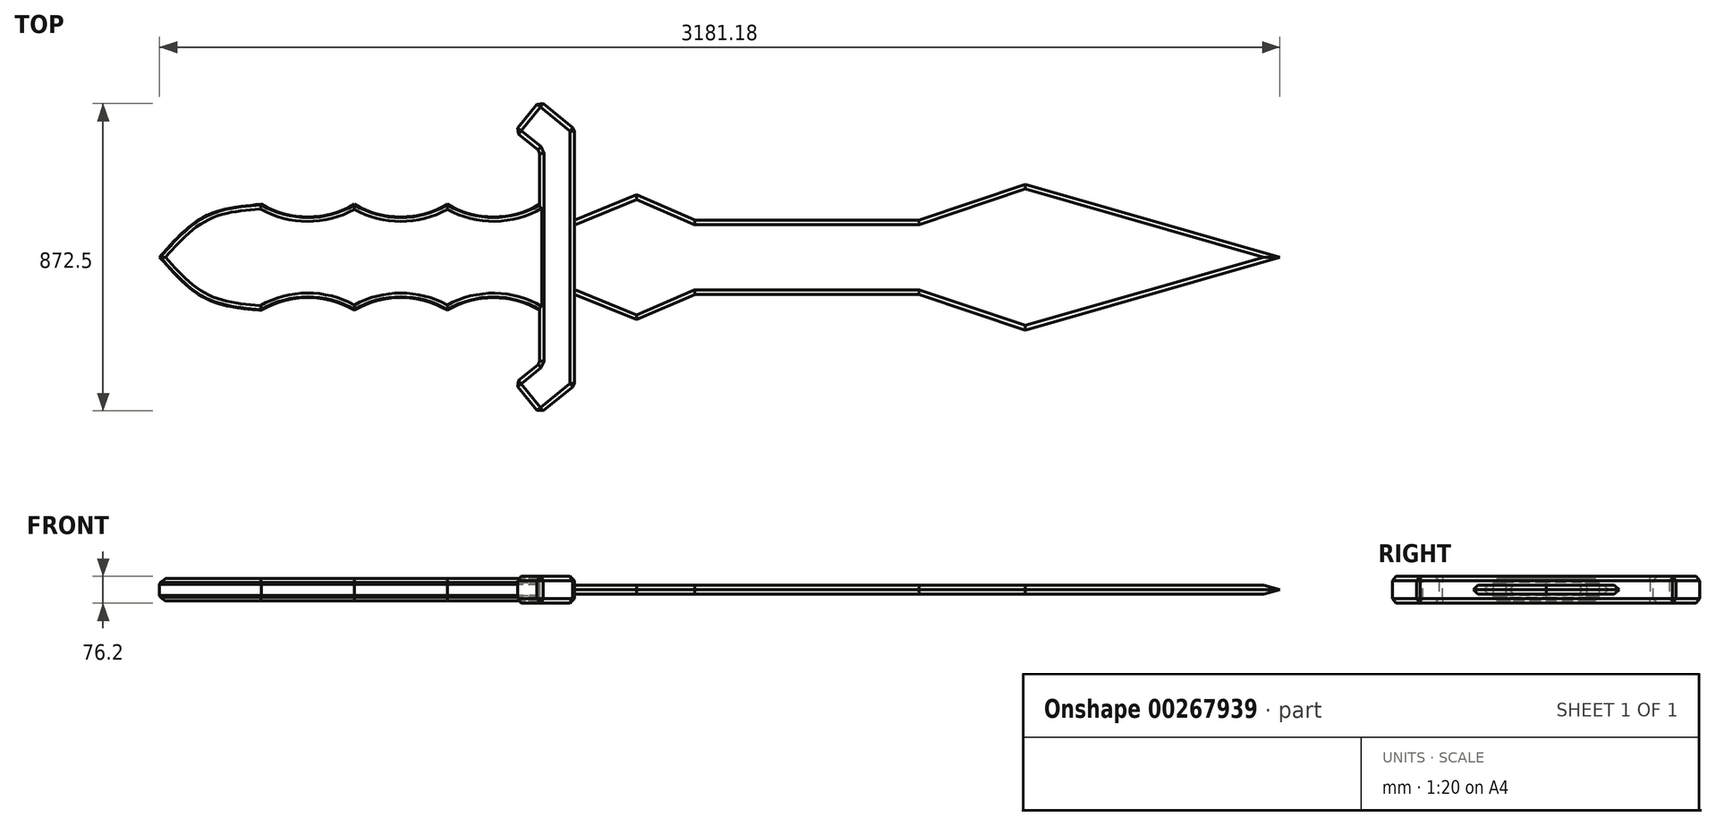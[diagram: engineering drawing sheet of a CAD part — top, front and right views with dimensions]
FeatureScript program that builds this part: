
annotation { "Feature Type Name" : "Feature", "Feature Type Description" : "" }
export const myFeature = defineFeature(function(context is Context, id is Id, definition is map)
    precondition{}
    {
        {
            var Q0;
            Q0=qCreatedBy(makeId("Top.planeOp"),FACE);
            var sketch = newSketch(context, id + "F0", { "sketchPlane" : qUnion([Q0])});
            skLineSegment(sketch, "E0", {"start": v(-1336.98, 0) * mm, "end": v(2042.28, 0) * mm, "construction": true});
            skLineSegment(sketch, "E1", {"start": v(2042.28, 0) * mm, "end": v(1319.26, 207.04) * mm});
            skLineSegment(sketch, "E2", {"start": v(1319.26, 207.04) * mm, "end": v(1016.82, 105.17) * mm});
            skLineSegment(sketch, "E3", {"start": v(1016.82, 105.17) * mm, "end": v(382.56, 105.17) * mm});
            skLineSegment(sketch, "E4", {"start": v(382.56, 105.17) * mm, "end": v(216.1, 177.22) * mm});
            skLineSegment(sketch, "E5", {"start": v(216.1, 177.22) * mm, "end": v(39.37, 105.17) * mm});
            skLineSegment(sketch, "E6", {"start": v(39.37, 105.17) * mm, "end": v(39.37, 0) * mm});
            skLineSegment(sketch, "E7", {"start": v(39.37, 105.17) * mm, "end": v(39.37, 364.38) * mm});
            skLineSegment(sketch, "E8", {"start": v(39.37, 364.38) * mm, "end": v(-59.33, 444.24) * mm});
            skLineSegment(sketch, "E9", {"start": v(-59.33, 444.24) * mm, "end": v(-129.5, 357.5) * mm});
            skLineSegment(sketch, "E10", {"start": v(-129.5, 357.5) * mm, "end": v(-59.33, 300.73) * mm});
            skLineSegment(sketch, "E11", {"start": v(-59.33, 300.73) * mm, "end": v(-59.33, 0) * mm});
            skArc(sketch, "E12", {"start": v(-321.86, 150.37) * mm, "mid": v(-190.6, 114.69) * mm, "end": v(-59.33, 150.37) * mm});
            skPoint(sketch, "E12.startSnap0", {"position": v(-59.33, 150.37) * mm});
            skArc(sketch, "E13", {"start": v(-585.75, 150.37) * mm, "mid": v(-453.8, 114.34) * mm, "end": v(-321.86, 150.37) * mm});
            skArc(sketch, "E14", {"start": v(-849.64, 150.37) * mm, "mid": v(-717.7, 114.34) * mm, "end": v(-585.75, 150.37) * mm});
            skLineSegment(sketch, "E15", {"start": v(-190.6, 374) * mm, "end": v(-1033.32, 374) * mm, "construction": true});
            skFitSpline(sketch, "E16", {"points": [v(-849.64, 150.37) * mm, v(-1008.23, 117.05) * mm, v(-1138.9, 0) * mm], "startDerivative": vector(-340.1, -28.4) * mm, "endDerivative": vector(-239.1, -270.74) * mm});
            skLineSegment(sketch, "E17.MirrorCS", {"start": v(1016.82, -105.17) * mm, "end": v(382.56, -105.17) * mm});
            skLineSegment(sketch, "E18.MirrorCS", {"start": v(1319.26, -207.04) * mm, "end": v(1016.82, -105.17) * mm});
            skLineSegment(sketch, "E19.MirrorCS", {"start": v(2042.28, 0) * mm, "end": v(1319.26, -207.04) * mm});
            skLineSegment(sketch, "E20.MirrorCS", {"start": v(216.1, -177.22) * mm, "end": v(39.37, -105.17) * mm});
            skLineSegment(sketch, "E21.MirrorCS", {"start": v(382.56, -105.17) * mm, "end": v(216.1, -177.22) * mm});
            skLineSegment(sketch, "E22.MirrorCS", {"start": v(39.37, -105.17) * mm, "end": v(39.37, 0) * mm});
            skLineSegment(sketch, "E23.MirrorCS", {"start": v(-59.33, -300.73) * mm, "end": v(-59.33, 0) * mm});
            skLineSegment(sketch, "E24.MirrorCS", {"start": v(39.37, -105.17) * mm, "end": v(39.37, -364.38) * mm});
            skLineSegment(sketch, "E25.MirrorCS", {"start": v(-129.5, -357.5) * mm, "end": v(-59.33, -300.73) * mm});
            skLineSegment(sketch, "E26.MirrorCS", {"start": v(-59.33, -444.24) * mm, "end": v(-129.5, -357.5) * mm});
            skLineSegment(sketch, "E27.MirrorCS", {"start": v(39.37, -364.38) * mm, "end": v(-59.33, -444.24) * mm});
            skArc(sketch, "E28.MirrorCS", {"start": v(-321.86, -150.37) * mm, "mid": v(-190.6, -114.69) * mm, "end": v(-59.33, -150.37) * mm});
            skArc(sketch, "E29.MirrorCS", {"start": v(-585.75, -150.37) * mm, "mid": v(-453.8, -114.34) * mm, "end": v(-321.86, -150.37) * mm});
            skArc(sketch, "E30.MirrorCS", {"start": v(-849.64, -150.37) * mm, "mid": v(-717.7, -114.34) * mm, "end": v(-585.75, -150.37) * mm});
            skFitSpline(sketch, "E31.MirrorCS", {"points": [v(-849.64, -150.37) * mm, v(-1008.23, -117.05) * mm, v(-1138.9, 0) * mm], "startDerivative": vector(-340.1, 28.4) * mm, "endDerivative": vector(-239.1, 270.74) * mm});
            skSolve(sketch);
        }
        {
            var Q0;
            Q0=makeQuery(id+"F0.imprint","IMPRINT",FACE,{"disambiguationData":[TD([[makeQuery(id+"F0.imprint","IMPRINT",EDGE,{"derivedFrom":sQuery(id+"F0.wireOp",EDGE,"E6")}),-1.0]])]});
            extrude(context, id + "F1", {"entities" : qUnion([Q0]), "depth" : 38.1 * mm, "hasSecondDirection" : true, "secondDirectionOppositeDirection" : true, "secondDirectionDepth" : 38.1 * mm});
        }
        {
            var Q0;
            {var subQ4=sQuery(id+"F0.wireOp",EDGE,"E12");Q0=makeQuery(id+"F0.imprint","IMPRINT",FACE,{"disambiguationData":[TD([[makeQuery(id+"F0.imprint","IMPRINT",EDGE,{"derivedFrom":subQ4}),-1.0]])]});}
            extrude(context, id + "F2", {"entities" : qUnion([Q0]), "operationType" : NewBodyOperationType.ADD, "depth" : 31.75 * mm, "hasSecondDirection" : true, "secondDirectionOppositeDirection" : true, "secondDirectionDepth" : 31.75 * mm});
        }
        {
            var Q0;
            Q0=makeQuery(id+"F0.imprint","IMPRINT",FACE,{"disambiguationData":[TD([[makeQuery(id+"F0.imprint","IMPRINT",EDGE,{"derivedFrom":sQuery(id+"F0.wireOp",EDGE,"E1")}),1.0]])]});
            extrude(context, id + "F3", {"entities" : qUnion([Q0]), "operationType" : NewBodyOperationType.ADD, "depth" : 12.7 * mm, "hasSecondDirection" : true, "secondDirectionOppositeDirection" : true, "secondDirectionDepth" : 12.7 * mm});
        }
        {
            var Q0;
            Q0=makeQuery(id+"F3.opExtrude","CAP_EDGE",EDGE,{"disambiguationData":[OSD([sQuery(id+"F0.wireOp",EDGE,"E5")])],"isStart":false});
            var Q1;
            Q1=makeQuery(id+"F3.opExtrude","CAP_EDGE",EDGE,{"disambiguationData":[OSD([sQuery(id+"F0.wireOp",EDGE,"E4")])],"isStart":false});
            var Q2;
            Q2=makeQuery(id+"F3.opExtrude","CAP_EDGE",EDGE,{"disambiguationData":[OSD([sQuery(id+"F0.wireOp",EDGE,"E3")])],"isStart":false});
            var Q3;
            Q3=makeQuery(id+"F3.opExtrude","CAP_EDGE",EDGE,{"disambiguationData":[OSD([sQuery(id+"F0.wireOp",EDGE,"E2")])],"isStart":false});
            var Q4;
            Q4=makeQuery(id+"F3.opExtrude","CAP_EDGE",EDGE,{"disambiguationData":[OSD([sQuery(id+"F0.wireOp",EDGE,"E1")])],"isStart":false});
            var Q5;
            Q5=makeQuery(id+"F3.opExtrude","CAP_EDGE",EDGE,{"disambiguationData":[OSD([sQuery(id+"F0.wireOp",EDGE,"E19.MirrorCS")])],"isStart":false});
            var Q6;
            Q6=makeQuery(id+"F3.opExtrude","CAP_EDGE",EDGE,{"disambiguationData":[OSD([sQuery(id+"F0.wireOp",EDGE,"E18.MirrorCS")])],"isStart":false});
            var Q7;
            Q7=makeQuery(id+"F3.opExtrude","CAP_EDGE",EDGE,{"disambiguationData":[OSD([sQuery(id+"F0.wireOp",EDGE,"E21.MirrorCS")])],"isStart":false});
            var Q8;
            Q8=makeQuery(id+"F3.opExtrude","CAP_EDGE",EDGE,{"disambiguationData":[OSD([sQuery(id+"F0.wireOp",EDGE,"E20.MirrorCS")])],"isStart":true});
            var Q9;
            Q9=makeQuery(id+"F3.opExtrude","CAP_EDGE",EDGE,{"disambiguationData":[OSD([sQuery(id+"F0.wireOp",EDGE,"E20.MirrorCS")])],"isStart":false});
            var Q10;
            Q10=makeQuery(id+"F3.opExtrude","CAP_EDGE",EDGE,{"disambiguationData":[OSD([sQuery(id+"F0.wireOp",EDGE,"E21.MirrorCS")])],"isStart":true});
            var Q11;
            Q11=makeQuery(id+"F3.opExtrude","CAP_EDGE",EDGE,{"disambiguationData":[OSD([sQuery(id+"F0.wireOp",EDGE,"E17.MirrorCS")])],"isStart":false});
            var Q12;
            Q12=makeQuery(id+"F3.opExtrude","CAP_EDGE",EDGE,{"disambiguationData":[OSD([sQuery(id+"F0.wireOp",EDGE,"E17.MirrorCS")])],"isStart":true});
            var Q13;
            Q13=makeQuery(id+"F3.opExtrude","CAP_EDGE",EDGE,{"disambiguationData":[OSD([sQuery(id+"F0.wireOp",EDGE,"E18.MirrorCS")])],"isStart":true});
            var Q14;
            Q14=makeQuery(id+"F3.opExtrude","CAP_EDGE",EDGE,{"disambiguationData":[OSD([sQuery(id+"F0.wireOp",EDGE,"E19.MirrorCS")])],"isStart":true});
            var Q15;
            Q15=makeQuery(id+"F3.opExtrude","CAP_EDGE",EDGE,{"disambiguationData":[OSD([sQuery(id+"F0.wireOp",EDGE,"E4")])],"isStart":true});
            var Q16;
            Q16=makeQuery(id+"F3.opExtrude","CAP_EDGE",EDGE,{"disambiguationData":[OSD([sQuery(id+"F0.wireOp",EDGE,"E5")])],"isStart":true});
            var Q17;
            Q17=makeQuery(id+"F3.opExtrude","CAP_EDGE",EDGE,{"disambiguationData":[OSD([sQuery(id+"F0.wireOp",EDGE,"E3")])],"isStart":true});
            var Q18;
            Q18=makeQuery(id+"F3.opExtrude","CAP_EDGE",EDGE,{"disambiguationData":[OSD([sQuery(id+"F0.wireOp",EDGE,"E2")])],"isStart":true});
            var Q19;
            Q19=makeQuery(id+"F3.opExtrude","CAP_EDGE",EDGE,{"disambiguationData":[OSD([sQuery(id+"F0.wireOp",EDGE,"E1")])],"isStart":true});
            chamfer(context, id + "F4", {"entities" : qUnion([Q0, Q1, Q2, Q3, Q4, Q5, Q6, Q7, Q8, Q9, Q10, Q11, Q12, Q13, Q14, Q15, Q16, Q17, Q18, Q19]), "width" : 12.7 * mm, "tangentPropagation" : true});
        }
        {
            var Q0;
            Q0=makeQuery(id+"F1.opExtrude","CAP_EDGE",EDGE,{"disambiguationData":[OSD([sQuery(id+"F0.wireOp",EDGE,"E11"),sQuery(id+"F0.wireOp",EDGE,"E23.MirrorCS")])],"isStart":false});
            var Q1;
            Q1=makeQuery(id+"F1.opExtrude","CAP_EDGE",EDGE,{"disambiguationData":[OSD([sQuery(id+"F0.wireOp",EDGE,"E10")])],"isStart":false});
            var Q2;
            Q2=makeQuery(id+"F1.opExtrude","CAP_EDGE",EDGE,{"disambiguationData":[OSD([sQuery(id+"F0.wireOp",EDGE,"E9")])],"isStart":false});
            var Q3;
            Q3=makeQuery(id+"F1.opExtrude","CAP_EDGE",EDGE,{"disambiguationData":[OSD([sQuery(id+"F0.wireOp",EDGE,"E8")])],"isStart":false});
            var Q4;
            Q4=makeQuery(id+"F1.opExtrude","CAP_EDGE",EDGE,{"disambiguationData":[OSD([sQuery(id+"F0.wireOp",EDGE,"E6"),sQuery(id+"F0.wireOp",EDGE,"E7"),sQuery(id+"F0.wireOp",EDGE,"E22.MirrorCS"),sQuery(id+"F0.wireOp",EDGE,"E24.MirrorCS")])],"isStart":false});
            var Q5;
            Q5=makeQuery(id+"F1.opExtrude","CAP_EDGE",EDGE,{"disambiguationData":[OSD([sQuery(id+"F0.wireOp",EDGE,"E25.MirrorCS")])],"isStart":false});
            var Q6;
            Q6=makeQuery(id+"F1.opExtrude","CAP_EDGE",EDGE,{"disambiguationData":[OSD([sQuery(id+"F0.wireOp",EDGE,"E26.MirrorCS")])],"isStart":false});
            var Q7;
            Q7=makeQuery(id+"F1.opExtrude","CAP_EDGE",EDGE,{"disambiguationData":[OSD([sQuery(id+"F0.wireOp",EDGE,"E27.MirrorCS")])],"isStart":false});
            var Q8;
            Q8=makeQuery(id+"F1.opExtrude","CAP_EDGE",EDGE,{"disambiguationData":[OSD([sQuery(id+"F0.wireOp",EDGE,"E27.MirrorCS")])],"isStart":true});
            var Q9;
            Q9=makeQuery(id+"F1.opExtrude","CAP_EDGE",EDGE,{"disambiguationData":[OSD([sQuery(id+"F0.wireOp",EDGE,"E26.MirrorCS")])],"isStart":true});
            var Q10;
            Q10=makeQuery(id+"F1.opExtrude","CAP_EDGE",EDGE,{"disambiguationData":[OSD([sQuery(id+"F0.wireOp",EDGE,"E6"),sQuery(id+"F0.wireOp",EDGE,"E7"),sQuery(id+"F0.wireOp",EDGE,"E22.MirrorCS"),sQuery(id+"F0.wireOp",EDGE,"E24.MirrorCS")])],"isStart":true});
            var Q11;
            Q11=makeQuery(id+"F1.opExtrude","CAP_EDGE",EDGE,{"disambiguationData":[OSD([sQuery(id+"F0.wireOp",EDGE,"E25.MirrorCS")])],"isStart":true});
            var Q12;
            Q12=makeQuery(id+"F1.opExtrude","CAP_EDGE",EDGE,{"disambiguationData":[OSD([sQuery(id+"F0.wireOp",EDGE,"E11"),sQuery(id+"F0.wireOp",EDGE,"E23.MirrorCS")])],"isStart":true});
            var Q13;
            Q13=makeQuery(id+"F1.opExtrude","CAP_EDGE",EDGE,{"disambiguationData":[OSD([sQuery(id+"F0.wireOp",EDGE,"E10")])],"isStart":true});
            var Q14;
            Q14=makeQuery(id+"F1.opExtrude","CAP_EDGE",EDGE,{"disambiguationData":[OSD([sQuery(id+"F0.wireOp",EDGE,"E9")])],"isStart":true});
            var Q15;
            Q15=makeQuery(id+"F1.opExtrude","CAP_EDGE",EDGE,{"disambiguationData":[OSD([sQuery(id+"F0.wireOp",EDGE,"E8")])],"isStart":true});
            var Q16;
            Q16=makeQuery(id+"F1.opExtrude","SWEPT_EDGE",EDGE,{"disambiguationData":[OSD([sQuery(id+"F0.wireOp",EDGE,"E26.MirrorCS"),sQuery(id+"F0.wireOp",EDGE,"E27.MirrorCS")])]});
            var Q17;
            Q17=makeQuery(id+"F1.opExtrude","SWEPT_EDGE",EDGE,{"disambiguationData":[OSD([sQuery(id+"F0.wireOp",EDGE,"E24.MirrorCS"),sQuery(id+"F0.wireOp",EDGE,"E27.MirrorCS")])]});
            var Q18;
            Q18=makeQuery(id+"F1.opExtrude","SWEPT_EDGE",EDGE,{"disambiguationData":[OSD([sQuery(id+"F0.wireOp",EDGE,"E25.MirrorCS"),sQuery(id+"F0.wireOp",EDGE,"E26.MirrorCS")])]});
            var Q19;
            Q19=makeQuery(id+"F1.opExtrude","SWEPT_EDGE",EDGE,{"disambiguationData":[OSD([sQuery(id+"F0.wireOp",EDGE,"E23.MirrorCS"),sQuery(id+"F0.wireOp",EDGE,"E25.MirrorCS")])]});
            var Q20;
            Q20=makeQuery(id+"F1.opExtrude","SWEPT_EDGE",EDGE,{"disambiguationData":[OSD([sQuery(id+"F0.wireOp",EDGE,"E10"),sQuery(id+"F0.wireOp",EDGE,"E11")])]});
            var Q21;
            Q21=makeQuery(id+"F1.opExtrude","SWEPT_EDGE",EDGE,{"disambiguationData":[OSD([sQuery(id+"F0.wireOp",EDGE,"E9"),sQuery(id+"F0.wireOp",EDGE,"E10")])]});
            var Q22;
            Q22=makeQuery(id+"F1.opExtrude","SWEPT_EDGE",EDGE,{"disambiguationData":[OSD([sQuery(id+"F0.wireOp",EDGE,"E7"),sQuery(id+"F0.wireOp",EDGE,"E8")])]});
            var Q23;
            Q23=makeQuery(id+"F1.opExtrude","SWEPT_EDGE",EDGE,{"disambiguationData":[OSD([sQuery(id+"F0.wireOp",EDGE,"E8"),sQuery(id+"F0.wireOp",EDGE,"E9")])]});
            chamfer(context, id + "F5", {"entities" : qUnion([Q0, Q1, Q2, Q3, Q4, Q5, Q6, Q7, Q8, Q9, Q10, Q11, Q12, Q13, Q14, Q15, Q16, Q17, Q18, Q19, Q20, Q21, Q22, Q23]), "width" : 12.7 * mm, "tangentPropagation" : true});
        }
        {
            var Q0;
            Q0=makeQuery(id+"F2.opExtrude","CAP_EDGE",EDGE,{"disambiguationData":[OSD([sQuery(id+"F0.wireOp",EDGE,"E30.MirrorCS")])],"isStart":false});
            var Q1;
            Q1=makeQuery(id+"F2.opExtrude","CAP_EDGE",EDGE,{"disambiguationData":[OSD([sQuery(id+"F0.wireOp",EDGE,"E30.MirrorCS")])],"isStart":true});
            var Q2;
            Q2=makeQuery(id+"F2.opExtrude","CAP_EDGE",EDGE,{"disambiguationData":[OSD([sQuery(id+"F0.wireOp",EDGE,"E29.MirrorCS")])],"isStart":true});
            var Q3;
            Q3=makeQuery(id+"F2.opExtrude","CAP_EDGE",EDGE,{"disambiguationData":[OSD([sQuery(id+"F0.wireOp",EDGE,"E29.MirrorCS")])],"isStart":false});
            var Q4;
            Q4=makeQuery(id+"F2.opExtrude","CAP_EDGE",EDGE,{"disambiguationData":[OSD([sQuery(id+"F0.wireOp",EDGE,"E28.MirrorCS")])],"isStart":false});
            var Q5;
            Q5=makeQuery(id+"F2.opExtrude","CAP_EDGE",EDGE,{"disambiguationData":[OSD([sQuery(id+"F0.wireOp",EDGE,"E28.MirrorCS")])],"isStart":true});
            var Q6;
            Q6=makeQuery(id+"F2.opExtrude","CAP_EDGE",EDGE,{"disambiguationData":[OSD([sQuery(id+"F0.wireOp",EDGE,"E12")])],"isStart":false});
            var Q7;
            Q7=makeQuery(id+"F2.opExtrude","CAP_EDGE",EDGE,{"disambiguationData":[OSD([sQuery(id+"F0.wireOp",EDGE,"E12")])],"isStart":true});
            var Q8;
            Q8=makeQuery(id+"F2.opExtrude","CAP_EDGE",EDGE,{"disambiguationData":[OSD([sQuery(id+"F0.wireOp",EDGE,"E13")])],"isStart":true});
            var Q9;
            Q9=makeQuery(id+"F2.opExtrude","CAP_EDGE",EDGE,{"disambiguationData":[OSD([sQuery(id+"F0.wireOp",EDGE,"E13")])],"isStart":false});
            var Q10;
            Q10=makeQuery(id+"F2.opExtrude","CAP_EDGE",EDGE,{"disambiguationData":[OSD([sQuery(id+"F0.wireOp",EDGE,"E14")])],"isStart":false});
            var Q11;
            Q11=makeQuery(id+"F2.opExtrude","CAP_EDGE",EDGE,{"disambiguationData":[OSD([sQuery(id+"F0.wireOp",EDGE,"E14")])],"isStart":true});
            chamfer(context, id + "F6", {"entities" : qUnion([Q0, Q1, Q2, Q3, Q4, Q5, Q6, Q7, Q8, Q9, Q10, Q11]), "width" : 12.7 * mm, "tangentPropagation" : true});
        }
        {
            var Q0;
            {var subQ0=sQuery(id+"F0.wireOp",EDGE,"E30.MirrorCS");Q0=makeQuery(id+"F6.opChamfer","BLEND_EDGE",EDGE,{"blendedFrom":[makeQuery(id+"F2.opExtrude","CAP_EDGE",EDGE,{"disambiguationData":[OSD([subQ0])],"isStart":false}),makeQuery(id+"F2.opExtrude","SWEPT_FACE",FACE,{"disambiguationData":[OSD([subQ0])]})],"blendedInto":[makeQuery(id+"F2.opExtrude","SWEPT_FACE",FACE,{"disambiguationData":[OSD([subQ0])]})]});}
            var Q1;
            {var subQ0=sQuery(id+"F0.wireOp",EDGE,"E30.MirrorCS");Q1=makeQuery(id+"F6.opChamfer","BLEND_EDGE",EDGE,{"blendedFrom":[makeQuery(id+"F2.opExtrude","CAP_EDGE",EDGE,{"disambiguationData":[OSD([subQ0])],"isStart":true}),makeQuery(id+"F2.opExtrude","SWEPT_FACE",FACE,{"disambiguationData":[OSD([subQ0])]})],"blendedInto":[makeQuery(id+"F2.opExtrude","SWEPT_FACE",FACE,{"disambiguationData":[OSD([subQ0])]})]});}
            var Q2;
            {var subQ0=sQuery(id+"F0.wireOp",EDGE,"E29.MirrorCS");Q2=makeQuery(id+"F6.opChamfer","BLEND_EDGE",EDGE,{"blendedFrom":[makeQuery(id+"F2.opExtrude","CAP_EDGE",EDGE,{"disambiguationData":[OSD([subQ0])],"isStart":true}),makeQuery(id+"F2.opExtrude","SWEPT_FACE",FACE,{"disambiguationData":[OSD([subQ0])]})],"blendedInto":[makeQuery(id+"F2.opExtrude","SWEPT_FACE",FACE,{"disambiguationData":[OSD([subQ0])]})]});}
            var Q3;
            {var subQ0=sQuery(id+"F0.wireOp",EDGE,"E29.MirrorCS");Q3=makeQuery(id+"F6.opChamfer","BLEND_EDGE",EDGE,{"blendedFrom":[makeQuery(id+"F2.opExtrude","CAP_EDGE",EDGE,{"disambiguationData":[OSD([subQ0])],"isStart":false}),makeQuery(id+"F2.opExtrude","SWEPT_FACE",FACE,{"disambiguationData":[OSD([subQ0])]})],"blendedInto":[makeQuery(id+"F2.opExtrude","SWEPT_FACE",FACE,{"disambiguationData":[OSD([subQ0])]})]});}
            var Q4;
            {var subQ0=sQuery(id+"F0.wireOp",EDGE,"E28.MirrorCS");Q4=makeQuery(id+"F6.opChamfer","BLEND_EDGE",EDGE,{"blendedFrom":[makeQuery(id+"F2.opExtrude","CAP_EDGE",EDGE,{"disambiguationData":[OSD([subQ0])],"isStart":false}),makeQuery(id+"F2.opExtrude","SWEPT_FACE",FACE,{"disambiguationData":[OSD([subQ0])]})],"blendedInto":[makeQuery(id+"F2.opExtrude","SWEPT_FACE",FACE,{"disambiguationData":[OSD([subQ0])]})]});}
            var Q5;
            {var subQ0=sQuery(id+"F0.wireOp",EDGE,"E28.MirrorCS");Q5=makeQuery(id+"F6.opChamfer","BLEND_EDGE",EDGE,{"blendedFrom":[makeQuery(id+"F2.opExtrude","CAP_EDGE",EDGE,{"disambiguationData":[OSD([subQ0])],"isStart":true}),makeQuery(id+"F2.opExtrude","SWEPT_FACE",FACE,{"disambiguationData":[OSD([subQ0])]})],"blendedInto":[makeQuery(id+"F2.opExtrude","SWEPT_FACE",FACE,{"disambiguationData":[OSD([subQ0])]})]});}
            var Q6;
            {var subQ0=sQuery(id+"F0.wireOp",EDGE,"E12");Q6=makeQuery(id+"F6.opChamfer","BLEND_EDGE",EDGE,{"blendedFrom":[makeQuery(id+"F2.opExtrude","CAP_EDGE",EDGE,{"disambiguationData":[OSD([subQ0])],"isStart":true}),makeQuery(id+"F2.opExtrude","SWEPT_FACE",FACE,{"disambiguationData":[OSD([subQ0])]})],"blendedInto":[makeQuery(id+"F2.opExtrude","SWEPT_FACE",FACE,{"disambiguationData":[OSD([subQ0])]})]});}
            var Q7;
            {var subQ0=sQuery(id+"F0.wireOp",EDGE,"E12");Q7=makeQuery(id+"F6.opChamfer","BLEND_EDGE",EDGE,{"blendedFrom":[makeQuery(id+"F2.opExtrude","CAP_EDGE",EDGE,{"disambiguationData":[OSD([subQ0])],"isStart":false}),makeQuery(id+"F2.opExtrude","SWEPT_FACE",FACE,{"disambiguationData":[OSD([subQ0])]})],"blendedInto":[makeQuery(id+"F2.opExtrude","SWEPT_FACE",FACE,{"disambiguationData":[OSD([subQ0])]})]});}
            var Q8;
            {var subQ0=sQuery(id+"F0.wireOp",EDGE,"E13");Q8=makeQuery(id+"F6.opChamfer","BLEND_EDGE",EDGE,{"blendedFrom":[makeQuery(id+"F2.opExtrude","CAP_EDGE",EDGE,{"disambiguationData":[OSD([subQ0])],"isStart":false}),makeQuery(id+"F2.opExtrude","SWEPT_FACE",FACE,{"disambiguationData":[OSD([subQ0])]})],"blendedInto":[makeQuery(id+"F2.opExtrude","SWEPT_FACE",FACE,{"disambiguationData":[OSD([subQ0])]})]});}
            var Q9;
            {var subQ0=sQuery(id+"F0.wireOp",EDGE,"E13");Q9=makeQuery(id+"F6.opChamfer","BLEND_EDGE",EDGE,{"blendedFrom":[makeQuery(id+"F2.opExtrude","CAP_EDGE",EDGE,{"disambiguationData":[OSD([subQ0])],"isStart":true}),makeQuery(id+"F2.opExtrude","SWEPT_FACE",FACE,{"disambiguationData":[OSD([subQ0])]})],"blendedInto":[makeQuery(id+"F2.opExtrude","SWEPT_FACE",FACE,{"disambiguationData":[OSD([subQ0])]})]});}
            var Q10;
            {var subQ0=sQuery(id+"F0.wireOp",EDGE,"E14");Q10=makeQuery(id+"F6.opChamfer","BLEND_EDGE",EDGE,{"blendedFrom":[makeQuery(id+"F2.opExtrude","CAP_EDGE",EDGE,{"disambiguationData":[OSD([subQ0])],"isStart":true}),makeQuery(id+"F2.opExtrude","SWEPT_FACE",FACE,{"disambiguationData":[OSD([subQ0])]})],"blendedInto":[makeQuery(id+"F2.opExtrude","SWEPT_FACE",FACE,{"disambiguationData":[OSD([subQ0])]})]});}
            var Q11;
            {var subQ0=sQuery(id+"F0.wireOp",EDGE,"E14");Q11=makeQuery(id+"F6.opChamfer","BLEND_EDGE",EDGE,{"blendedFrom":[makeQuery(id+"F2.opExtrude","CAP_EDGE",EDGE,{"disambiguationData":[OSD([subQ0])],"isStart":false}),makeQuery(id+"F2.opExtrude","SWEPT_FACE",FACE,{"disambiguationData":[OSD([subQ0])]})],"blendedInto":[makeQuery(id+"F2.opExtrude","SWEPT_FACE",FACE,{"disambiguationData":[OSD([subQ0])]})]});}
            chamfer(context, id + "F7", {"entities" : qUnion([Q0, Q1, Q2, Q3, Q4, Q5, Q6, Q7, Q8, Q9, Q10, Q11]), "width" : 6.35 * mm, "tangentPropagation" : true});
        }
        {
            var Q0;
            Q0=makeQuery(id+"F2.opExtrude","CAP_EDGE",EDGE,{"disambiguationData":[OSD([sQuery(id+"F0.wireOp",EDGE,"E31.MirrorCS")])],"isStart":false});
            var Q1;
            Q1=makeQuery(id+"F2.opExtrude","CAP_EDGE",EDGE,{"disambiguationData":[OSD([sQuery(id+"F0.wireOp",EDGE,"E31.MirrorCS")])],"isStart":true});
            var Q2;
            Q2=makeQuery(id+"F2.opExtrude","CAP_EDGE",EDGE,{"disambiguationData":[OSD([sQuery(id+"F0.wireOp",EDGE,"E16")])],"isStart":false});
            var Q3;
            Q3=makeQuery(id+"F2.opExtrude","CAP_EDGE",EDGE,{"disambiguationData":[OSD([sQuery(id+"F0.wireOp",EDGE,"E16")])],"isStart":true});
            chamfer(context, id + "F8", {"entities" : qUnion([Q0, Q1, Q2, Q3]), "width" : 12.7 * mm, "tangentPropagation" : true});
        }
        {
            var Q0;
            {var subQ0=sQuery(id+"F0.wireOp",EDGE,"E31.MirrorCS");Q0=makeQuery(id+"F8.opChamfer","BLEND_EDGE",EDGE,{"blendedFrom":[makeQuery(id+"F2.opExtrude","CAP_EDGE",EDGE,{"disambiguationData":[OSD([subQ0])],"isStart":false}),makeQuery(id+"F2.opExtrude","SWEPT_FACE",FACE,{"disambiguationData":[OSD([subQ0])]})],"blendedInto":[makeQuery(id+"F2.opExtrude","SWEPT_FACE",FACE,{"disambiguationData":[OSD([subQ0])]})]});}
            var Q1;
            {var subQ0=sQuery(id+"F0.wireOp",EDGE,"E31.MirrorCS");Q1=makeQuery(id+"F8.opChamfer","BLEND_EDGE",EDGE,{"blendedFrom":[makeQuery(id+"F2.opExtrude","CAP_EDGE",EDGE,{"disambiguationData":[OSD([subQ0])],"isStart":true}),makeQuery(id+"F2.opExtrude","SWEPT_FACE",FACE,{"disambiguationData":[OSD([subQ0])]})],"blendedInto":[makeQuery(id+"F2.opExtrude","SWEPT_FACE",FACE,{"disambiguationData":[OSD([subQ0])]})]});}
            var Q2;
            {var subQ0=sQuery(id+"F0.wireOp",EDGE,"E16");Q2=makeQuery(id+"F8.opChamfer","BLEND_EDGE",EDGE,{"blendedFrom":[makeQuery(id+"F2.opExtrude","CAP_EDGE",EDGE,{"disambiguationData":[OSD([subQ0])],"isStart":true}),makeQuery(id+"F2.opExtrude","SWEPT_FACE",FACE,{"disambiguationData":[OSD([subQ0])]})],"blendedInto":[makeQuery(id+"F2.opExtrude","SWEPT_FACE",FACE,{"disambiguationData":[OSD([subQ0])]})]});}
            var Q3;
            {var subQ0=sQuery(id+"F0.wireOp",EDGE,"E16");Q3=makeQuery(id+"F8.opChamfer","BLEND_EDGE",EDGE,{"blendedFrom":[makeQuery(id+"F2.opExtrude","CAP_EDGE",EDGE,{"disambiguationData":[OSD([subQ0])],"isStart":false}),makeQuery(id+"F2.opExtrude","SWEPT_FACE",FACE,{"disambiguationData":[OSD([subQ0])]})],"blendedInto":[makeQuery(id+"F2.opExtrude","SWEPT_FACE",FACE,{"disambiguationData":[OSD([subQ0])]})]});}
            chamfer(context, id + "F9", {"entities" : qUnion([Q0, Q1, Q2, Q3]), "width" : 6.35 * mm, "tangentPropagation" : true});
        }
    });
